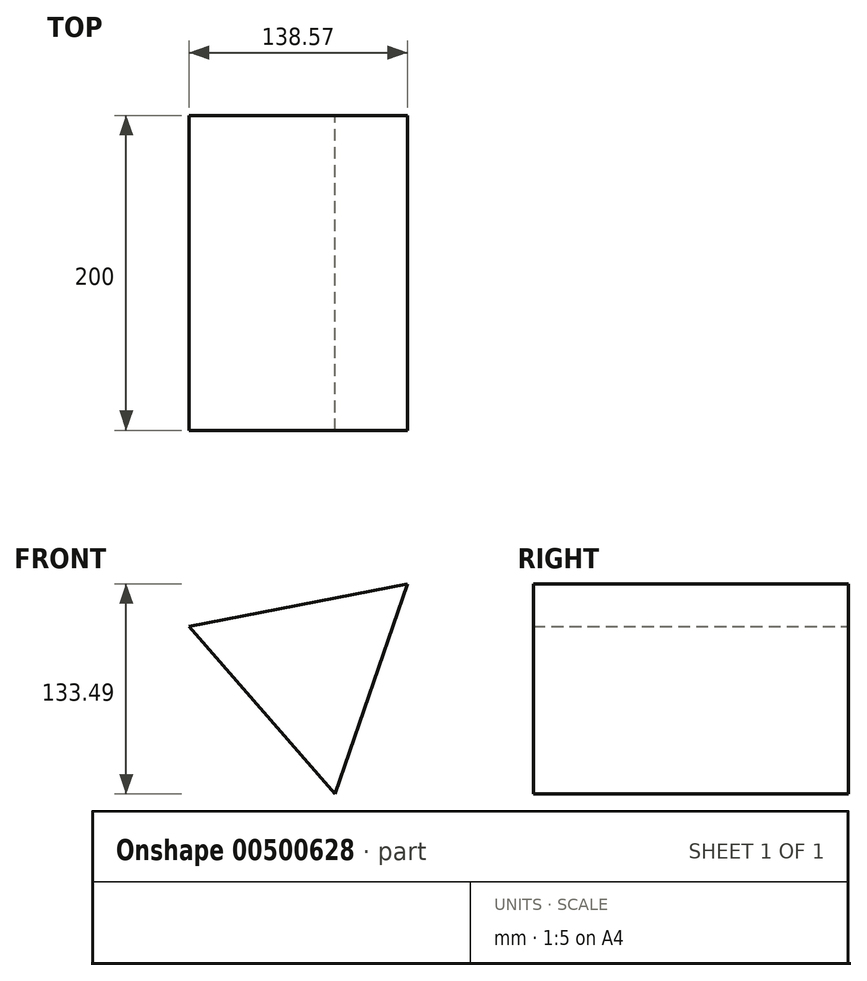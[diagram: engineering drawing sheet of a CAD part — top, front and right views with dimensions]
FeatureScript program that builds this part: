
annotation { "Feature Type Name" : "Feature", "Feature Type Description" : "" }
export const myFeature = defineFeature(function(context is Context, id is Id, definition is map)
    precondition{}
    {
        {
            var Q0;
            Q0=qCreatedBy(makeId("Front.planeOp"),FACE);
            var sketch = newSketch(context, id + "F0", { "sketchPlane" : qUnion([Q0])});
            skCircle(sketch, "E0.cCircle", {"center": v(0, 0) * mm, "radius": 81.5 * mm, "construction": true});
            skLineSegment(sketch, "E0.0", {"start": v(61.5, 53.49) * mm, "end": v(15.57, -80) * mm});
            skLineSegment(sketch, "E0.1", {"start": v(15.57, -80) * mm, "end": v(-77.07, 26.52) * mm});
            skLineSegment(sketch, "E0.2", {"start": v(-77.07, 26.52) * mm, "end": v(61.5, 53.49) * mm});
            skSolve(sketch);
        }
        {
            var Q0;
            Q0=makeQuery(id+"F0.imprint","IMPRINT",FACE,{"disambiguationData":[TD([[makeQuery(id+"F0.imprint","IMPRINT",EDGE,{"derivedFrom":sQuery(id+"F0.wireOp",EDGE,"E0.0")}),-1.0]])]});
            extrude(context, id + "F1", {"entities" : qUnion([Q0]), "depth" : 200 * mm});
        }
    });
